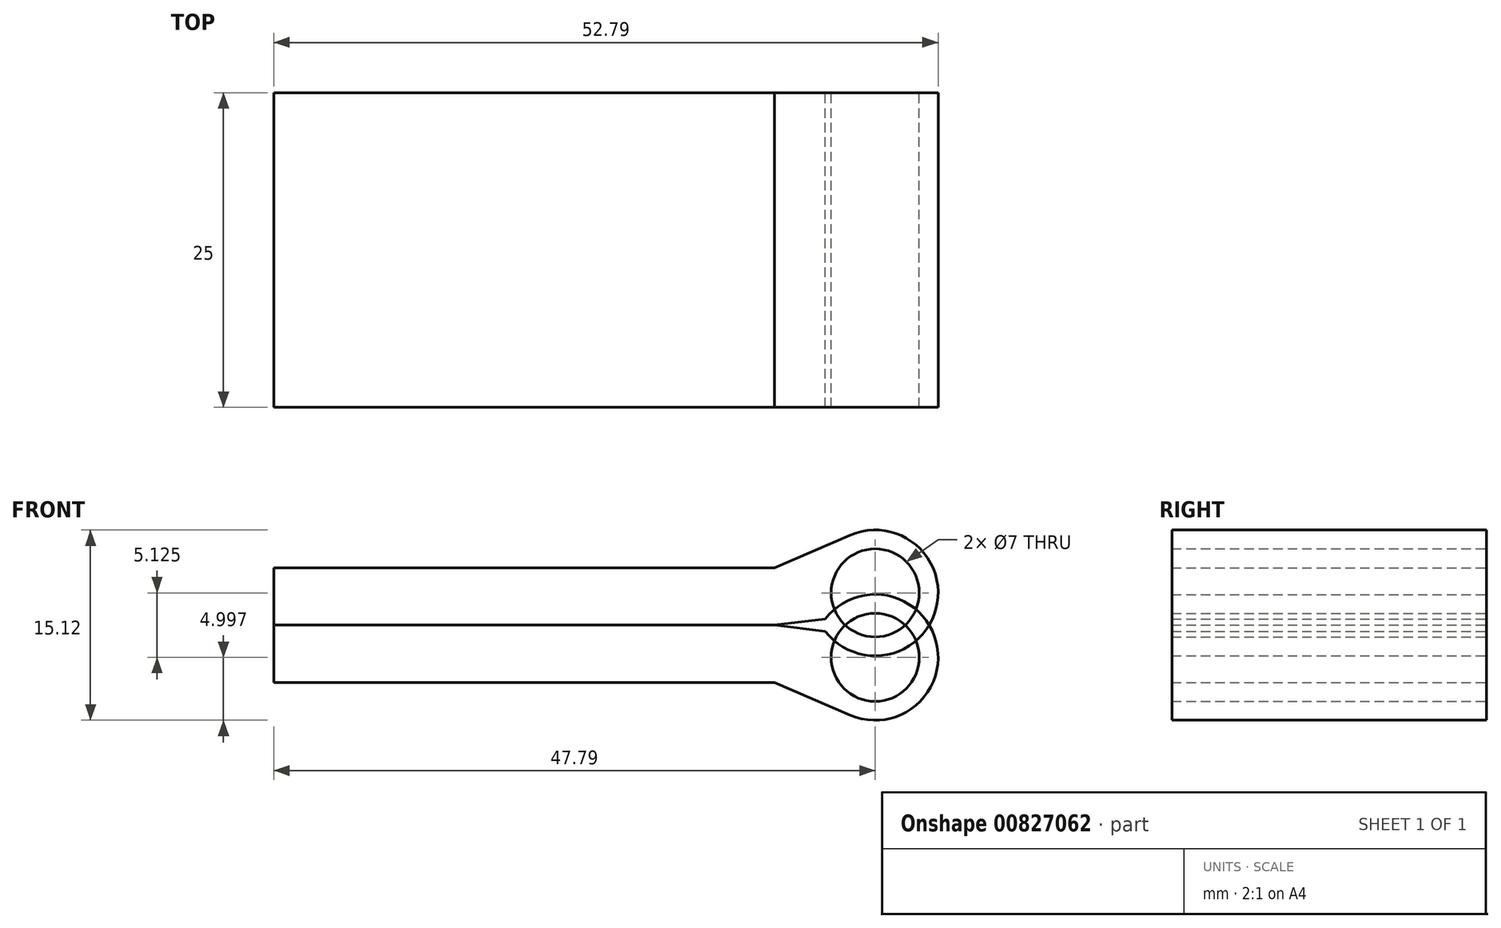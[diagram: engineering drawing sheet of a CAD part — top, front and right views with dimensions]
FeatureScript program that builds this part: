
annotation { "Feature Type Name" : "Feature", "Feature Type Description" : "" }
export const myFeature = defineFeature(function(context is Context, id is Id, definition is map)
    precondition{}
    {
        {
            var Q0;
            Q0=qCreatedBy(makeId("Front.planeOp"),FACE);
            var sketch = newSketch(context, id + "F0", { "sketchPlane" : qUnion([Q0])});
            skLineSegment(sketch, "E0.bottom", {"start": v(-20.94, 0) * mm, "end": v(18.85, 0) * mm});
            skLineSegment(sketch, "E0.top", {"start": v(-20.94, -4.56) * mm, "end": v(18.85, -4.56) * mm});
            skLineSegment(sketch, "E0.left", {"start": v(-20.94, 0) * mm, "end": v(-20.94, -4.56) * mm});
            skLineSegment(sketch, "E0.right", {"start": v(18.85, 0) * mm, "end": v(18.85, -4.56) * mm});
            skArc(sketch, "E1", {"start": v(24.87, -7.16) * mm, "mid": v(31.69, -1.3) * mm, "end": v(22.89, 0.49) * mm});
            skCircle(sketch, "E2", {"center": v(26.85, -2.56) * mm, "radius": 3.5 * mm});
            skLineSegment(sketch, "E3", {"start": v(18.85, -4.56) * mm, "end": v(24.87, -7.16) * mm});
            skLineSegment(sketch, "E4", {"start": v(18.85, 0) * mm, "end": v(26.43, 0.91) * mm});
            skSolve(sketch);
        }
        {
            var Q0;
            Q0=makeQuery(id+"F0.imprint","IMPRINT",FACE,{"disambiguationData":[TD([[makeQuery(id+"F0.imprint","IMPRINT",EDGE,{"derivedFrom":sQuery(id+"F0.wireOp",EDGE,"E0.bottom")}),-1.0]])]});
            var Q1;
            {var subQ1=sQuery(id+"F0.wireOp",EDGE,"E0.right");Q1=makeQuery(id+"F0.imprint","IMPRINT",FACE,{"disambiguationData":[TD([[makeQuery(id+"F0.imprint","IMPRINT",EDGE,{"derivedFrom":subQ1}),1.0]])]});}
            extrude(context, id + "F1", {"entities" : qUnion([Q0, Q1]), "depth" : 25 * mm, "offsetDistance" : 25 * mm});
        }
        {
            var Q0;
            Q0=qCreatedBy(makeId("Top.planeOp"),FACE);
            cPlane(context, id + "F2", {"entities" : qUnion([Q0]), "cplaneType" : CPlaneType.OFFSET, "offset" : 0 * mm, "width" : 150 * mm, "height" : 150 * mm});
        }
        {
            var Q0;
            Q0=makeQuery(id+"F1.opExtrude","SWEPT_BODY",BODY,{"disambiguationData":[OSD([sQuery(id+"F0.wireOp",EDGE,"E0.bottom"),sQuery(id+"F0.wireOp",EDGE,"E0.top"),sQuery(id+"F0.wireOp",EDGE,"E0.left"),sQuery(id+"F0.wireOp",EDGE,"E1"),sQuery(id+"F0.wireOp",EDGE,"E2"),sQuery(id+"F0.wireOp",EDGE,"E3"),sQuery(id+"F0.wireOp",EDGE,"E4")])]});
            var Q1;
            Q1=qCreatedBy(id+"F2.planeOp",FACE);
            mirror(context, id + "F3", {"entities" : qUnion([Q0]), "mirrorPlane" : qUnion([Q1])});
        }
    });
